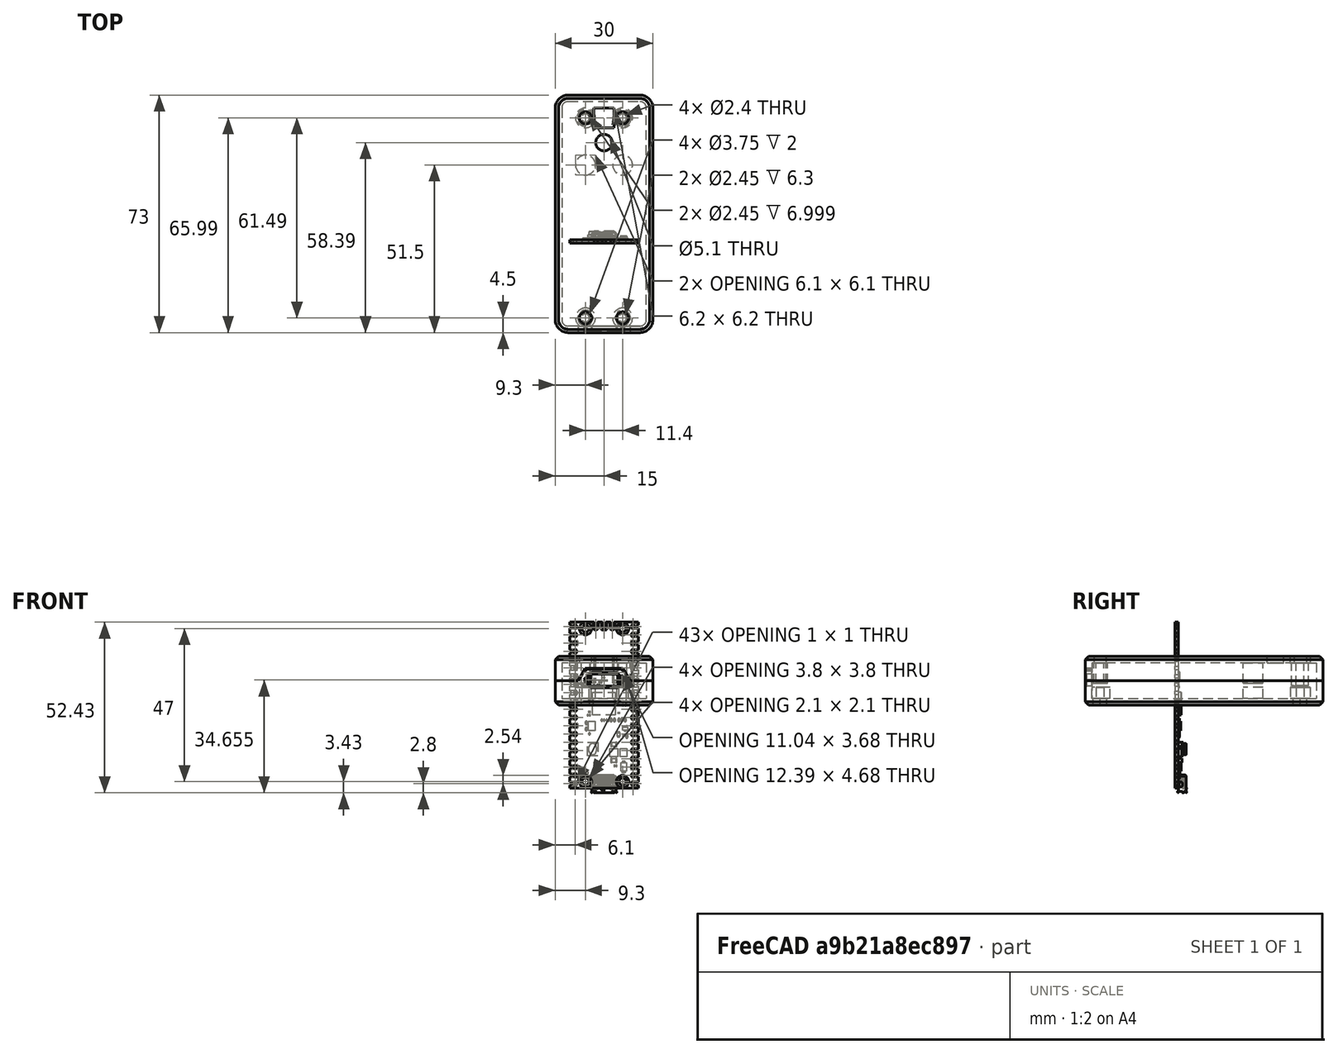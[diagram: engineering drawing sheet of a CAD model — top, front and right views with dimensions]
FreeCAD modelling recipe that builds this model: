
FCSTD DOCUMENT  (FreeCAD 2022.111R30764 (Git))
Label: case
License: All rights reserved
LicenseURL: http://en.wikipedia.org/wiki/All_rights_reserved
objects: Part::Feature×44, Sketcher::SketchObject×18, PartDesign::SubShapeBinder×13, PartDesign::Pocket×9, PartDesign::Pad×7, PartDesign::Chamfer×5, PartDesign::Extrusion×4, PartDesign::Body×4, App::Part×2, PartDesign::Fillet×2, PartDesign::Plane×2, Mesh::Feature×2, PartDesign::Solid×2, PartDesign::Thickness×1, PartDesign::ShapeBinder×1, PartDesign::Split×1
note: 170 computed .brp shape members not serialized (recipe doc carries the construction recipe); baked Part::Feature solids carry a one-line shape summary decoded from their .brp

FEATURE [Part::Feature] Part__Feature  label="PCB, Raspberry Pi Pico-R3"
  TreeRank = 93
  shape: bbox 21 x 1 x 51 mm, 416 faces (baked)
FEATURE [Part::Feature] Part__Feature001  label="MicroUSB Port, Raspberry Pi Pico-R3"
  Placement = pos=(0,0.5,-24.35) rot=(0,1,0;3.14159rad)
  TreeRank = 94
  shape: bbox 8 x 2.95 x 5.462 mm, 1230 faces, 7 solids (baked)
FEATURE [Part::Feature] Part__Feature002  label="RP2040 Microcontroller, Raspberry Pi Pico-R3"
  Placement = pos=(0,0.5,0.5) rot=(0,0,1;0rad)
  TreeRank = 95
  shape: bbox 7 x 0.9 x 7 mm, 6 faces (baked)
FEATURE [Part::Feature] Part__Feature003  label="SW1, Tact Switch, Raspberry Pi Pico-R3"
  Placement = pos=(-3.5,0.5,-13.5) rot=(0,0,1;0rad)
  TreeRank = 96
  shape: bbox 3.2 x 2.5 x 4.25 mm, 17 faces (baked)
FEATURE [Part::Feature] Part__Feature004  label="D1, Diode, Schottky, Raspberry Pi Pico-R3"
  Placement = pos=(6,0.5,-19) rot=(0,0,1;0rad)
  TreeRank = 97
  shape: bbox 1.65 x 0.95 x 3.6 mm, 14 faces (baked)
FEATURE [Part::Feature] Part__Feature005  label="D2, QSME-C194, LED, Raspberry Pi Pico-R3"
  Placement = pos=(-5.8,0.5,-20.8) rot=(0,0,1;0rad)
  TreeRank = 98
  shape: bbox 1.6 x 0.55 x 0.8 mm, 6 faces (baked)
FEATURE [Part::Feature] Part__Feature006  label="L1, Inductor, Raspberry Pi Pico-R3"
  Placement = pos=(6,0.5,-14.6) rot=(0,0,1;0rad)
  TreeRank = 99
  shape: bbox 2 x 1.2 x 2.5 mm, 6 faces (baked)
FEATURE [Part::Feature] Part__Feature007  label="U2, RT6150B-33GQW, Buck Boost Converter, Raspberry Pi Pico-R3"
  Placement = pos=(3,0.5,-14.6) rot=(0,0,1;0rad)
  TreeRank = 100
  shape: bbox 2.5 x 0.8 x 2.5 mm, 6 faces (baked)
FEATURE [Part::Feature] Part__Feature008  label="U3, W25Q16JVUXIQ, Serial NOR Flash 16 Mbit, Raspberry Pi Pico-R3"
  Placement = pos=(-3.8,0.5,-6.4) rot=(0,0,1;0rad)
  TreeRank = 101
  shape: bbox 2 x 0.8 x 3 mm, 6 faces (baked)
FEATURE [Part::Feature] Part__Feature009  label="Q1, MOSFET, DMG1012T, Raspberry Pi Pico-R3"
  Placement = pos=(6.5,0.5,-7.2) rot=(0,0,1;0rad)
  TreeRank = 102
  shape: bbox 1.6 x 0.6 x 1.8 mm, 18 faces (baked)
FEATURE [Part::Feature] Part__Feature010  label="X1, X12M000000S096, 12 Mhz Crystal Resonator, Raspberry Pi Pico-R3"
  Placement = pos=(-2.2,0.5,9) rot=(0,0,1;0rad)
  TreeRank = 103
  shape: bbox 3.2 x 0.6 x 2.5 mm, 18 faces (baked)
FEATURE [Part::Feature] Part__Feature011  label="SMD Resistor, Configurable, Raspberry Pi Pico-R3_R1"
  Placement = pos=(6.2,0.5,1) rot=(0,1,0;1.5708rad)
  TreeRank = 104
  shape: bbox 1 x 0.35 x 0.5 mm, 18 faces, 3 solids (baked)
FEATURE [Part::Feature] Part__Feature012  label="SMD Resistor, Configurable, Raspberry Pi Pico-R3_R2"
  Placement = pos=(3.5,0.5,-18.6) rot=(0,1,0;1.5708rad)
  TreeRank = 105
  shape: bbox 1 x 0.35 x 0.5 mm, 18 faces, 3 solids (baked)
FEATURE [Part::Feature] Part__Feature013  label="SMD Resistor, Configurable, Raspberry Pi Pico-R3_R3"
  Placement = pos=(-2.7,0.5,-17.8) rot=(0,1,0;1.5708rad)
  TreeRank = 106
  shape: bbox 1 x 0.35 x 0.5 mm, 18 faces, 3 solids (baked)
FEATURE [Part::Feature] Part__Feature014  label="SMD Resistor, Configurable, Raspberry Pi Pico-R3_R4"
  Placement = pos=(-5.5,0.5,-5.4) rot=(0,1,0;3.14159rad)
  TreeRank = 107
  shape: bbox 0.5 x 0.35 x 1 mm, 18 faces, 3 solids (baked)
FEATURE [Part::Feature] Part__Feature015  label="SMD Resistor, Configurable, Raspberry Pi Pico-R3_R5"
  Placement = pos=(7,0.5,-9.6) rot=(0,1,0;3.14159rad)
  TreeRank = 108
  shape: bbox 0.5 x 0.35 x 1 mm, 18 faces, 3 solids (baked)
FEATURE [Part::Feature] Part__Feature016  label="SMD Resistor, Configurable, Raspberry Pi Pico-R3_R6"
  Placement = pos=(6.5,0.5,-4.6) rot=(0,1,0;3.14159rad)
  TreeRank = 109
  shape: bbox 0.5 x 0.35 x 1 mm, 18 faces, 3 solids (baked)
FEATURE [Part::Feature] Part__Feature017  label="SMD Resistor, Configurable, Raspberry Pi Pico-R3_R7"
  Placement = pos=(4.5,0.5,-9) rot=(0,1,0;3.14159rad)
  TreeRank = 110
  shape: bbox 0.8 x 0.45 x 1.6 mm, 18 faces, 3 solids (baked)
FEATURE [Part::Feature] Part__Feature018  label="SMD Resistor, Configurable, Raspberry Pi Pico-R3_R8"
  Placement = pos=(-2.7,0.5,-18.8) rot=(0,1,0;1.5708rad)
  TreeRank = 111
  shape: bbox 1 x 0.35 x 0.5 mm, 18 faces, 3 solids (baked)
FEATURE [Part::Feature] Part__Feature019  label="SMD Resistor, Configurable, Raspberry Pi Pico-R3_R9"
  Placement = pos=(5.5,0.5,-4.6) rot=(0,1,0;3.14159rad)
  TreeRank = 112
  shape: bbox 0.5 x 0.35 x 1 mm, 18 faces, 3 solids (baked)
FEATURE [Part::Feature] Part__Feature020  label="SMD Resistor, Configurable, Raspberry Pi Pico-R3_R10"
  Placement = pos=(6.2,0.5,-1e-16) rot=(0,1,0;1.5708rad)
  TreeRank = 113
  shape: bbox 1 x 0.35 x 0.5 mm, 18 faces, 3 solids (baked)
FEATURE [Part::Feature] Part__Feature021  label="SMD Resistor, Configurable, Raspberry Pi Pico-R3_R11"
  Placement = pos=(-5.5,0.5,-7.4) rot=(0,0,1;0rad)
  TreeRank = 114
  shape: bbox 0.5 x 0.35 x 1 mm, 18 faces, 3 solids (baked)
FEATURE [Part::Feature] Part__Feature022  label="SMD Resistor, Configurable, Raspberry Pi Pico-R3_R12"
  Placement = pos=(0.8,0.5,-4.6) rot=(0,1,0;3.14159rad)
  TreeRank = 115
  shape: bbox 0.3 x 0.23 x 0.6 mm, 18 faces, 3 solids (baked)
FEATURE [Part::Feature] Part__Feature023  label="SMD Resistor, Configurable, Raspberry Pi Pico-R3_R13"
  Placement = pos=(1.4,0.5,-4.6) rot=(0,1,0;3.14159rad)
  TreeRank = 116
  shape: bbox 0.3 x 0.23 x 0.6 mm, 18 faces, 3 solids (baked)
FEATURE [Part::Feature] Part__Feature024  label="SMD Resistor, Configurable, Raspberry Pi Pico-R3_R14"
  Placement = pos=(-1.1,0.5,7) rot=(0,1,0;1.5708rad)
  TreeRank = 117
  shape: bbox 1 x 0.35 x 0.5 mm, 18 faces, 3 solids (baked)
FEATURE [Part::Feature] Part__Feature025  label="SMD Resistor, Configurable, Raspberry Pi Pico-R3_R15"
  Placement = pos=(-1.7,0.5,6.2) rot=(0,1,0;1.5708rad)
  TreeRank = 118
  shape: bbox 1 x 0.35 x 0.5 mm, 18 faces, 3 solids (baked)
FEATURE [Part::Feature] Part__Feature026  label="SMD Capacitor, Configurable, Raspberry Pi Pico-R3_C1"
  Placement = pos=(3,0.5,-17) rot=(0,1,0;1.5708rad)
  TreeRank = 119
  shape: bbox 2 x 1.25 x 1.25 mm, 18 faces, 3 solids (baked)
FEATURE [Part::Feature] Part__Feature027  label="SMD Capacitor, Configurable, Raspberry Pi Pico-R3_C2"
  Placement = pos=(3,0.5,-12) rot=(0,1,0;1.5708rad)
  TreeRank = 120
  shape: bbox 2 x 1.25 x 1.25 mm, 18 faces, 3 solids (baked)
FEATURE [Part::Feature] Part__Feature028  label="SMD Capacitor, Configurable, Raspberry Pi Pico-R3_C3"
  Placement = pos=(6,0.5,-9.4) rot=(0,0,1;0rad)
  TreeRank = 121
  shape: bbox 0.3 x 0.3 x 0.6 mm, 18 faces, 3 solids (baked)
FEATURE [Part::Feature] Part__Feature029  label="SMD Capacitor, Configurable, Raspberry Pi Pico-R3_C4"
  Placement = pos=(-4.5,0.5,-2.1) rot=(0,-1,0;1.5708rad)
  TreeRank = 122
  shape: bbox 0.6 x 0.3 x 0.3 mm, 18 faces, 3 solids (baked)
FEATURE [Part::Feature] Part__Feature030  label="SMD Capacitor, Configurable, Raspberry Pi Pico-R3_C5"
  Placement = pos=(-4.5,0.5,1.5) rot=(0,-1,0;1.5708rad)
  TreeRank = 123
  shape: bbox 0.6 x 0.3 x 0.3 mm, 18 faces, 3 solids (baked)
FEATURE [Part::Feature] Part__Feature031  label="SMD Capacitor, Configurable, Raspberry Pi Pico-R3_C6"
  Placement = pos=(4.6,0.5,1.9) rot=(0,1,0;0.785398rad)
  TreeRank = 124
  shape: bbox 0.6364 x 0.3 x 0.6364 mm, 18 faces, 3 solids (baked)
FEATURE [Part::Feature] Part__Feature032  label="SMD Capacitor, Configurable, Raspberry Pi Pico-R3_C7"
  Placement = pos=(4.5,0.5,-2.4) rot=(0,-1,0;1.5708rad)
  TreeRank = 125
  shape: bbox 0.6 x 0.3 x 0.3 mm, 18 faces, 3 solids (baked)
FEATURE [Part::Feature] Part__Feature033  label="SMD Capacitor, Configurable, Raspberry Pi Pico-R3_C8"
  Placement = pos=(0,0.5,5.5) rot=(0,0,1;0rad)
  TreeRank = 126
  shape: bbox 0.3 x 0.3 x 0.6 mm, 18 faces, 3 solids (baked)
FEATURE [Part::Feature] Part__Feature034  label="SMD Capacitor, Configurable, Raspberry Pi Pico-R3_C9"
  Placement = pos=(0.8,0.5,5.5) rot=(0,0,1;0rad)
  TreeRank = 127
  shape: bbox 0.3 x 0.3 x 0.6 mm, 18 faces, 3 solids (baked)
FEATURE [Part::Feature] Part__Feature035  label="SMD Capacitor, Configurable, Raspberry Pi Pico-R3_C10"
  Placement = pos=(0,0.5,-4.6) rot=(0,0,1;0rad)
  TreeRank = 128
  shape: bbox 0.3 x 0.3 x 0.6 mm, 18 faces, 3 solids (baked)
FEATURE [Part::Feature] Part__Feature036  label="SMD Capacitor, Configurable, Raspberry Pi Pico-R3_C11"
  Placement = pos=(-0.7,0.5,-4.6) rot=(0,0,1;0rad)
  TreeRank = 129
  shape: bbox 0.3 x 0.3 x 0.6 mm, 18 faces, 3 solids (baked)
FEATURE [Part::Feature] Part__Feature037  label="SMD Capacitor, Configurable, Raspberry Pi Pico-R3_C12"
  Placement = pos=(2.2,0.5,-4.6) rot=(0,0,1;0rad)
  TreeRank = 130
  shape: bbox 0.5 x 0.5 x 1 mm, 18 faces, 3 solids (baked)
FEATURE [Part::Feature] Part__Feature038  label="SMD Capacitor, Configurable, Raspberry Pi Pico-R3_C13"
  Placement = pos=(4.6,0.5,-4.6) rot=(0,0,1;0rad)
  TreeRank = 131
  shape: bbox 0.5 x 0.5 x 1 mm, 18 faces, 3 solids (baked)
FEATURE [Part::Feature] Part__Feature039  label="SMD Capacitor, Configurable, Raspberry Pi Pico-R3_C14"
  Placement = pos=(3.2,0.5,-4.6) rot=(0,0,1;0rad)
  TreeRank = 132
  shape: bbox 0.5 x 0.5 x 1 mm, 18 faces, 3 solids (baked)
FEATURE [Part::Feature] Part__Feature040  label="SMD Capacitor, Configurable, Raspberry Pi Pico-R3_C15"
  Placement = pos=(-4.5,0.5,-8.8) rot=(0,0,1;0rad)
  TreeRank = 133
  shape: bbox 0.3 x 0.3 x 0.6 mm, 18 faces, 3 solids (baked)
FEATURE [Part::Feature] Part__Feature041  label="SMD Capacitor, Configurable, Raspberry Pi Pico-R3_C16"
  Placement = pos=(-4.6,0.5,9.6) rot=(0,0,1;0rad)
  TreeRank = 134
  shape: bbox 0.3 x 0.3 x 0.6 mm, 18 faces, 3 solids (baked)
FEATURE [Part::Feature] Part__Feature042  label="SMD Capacitor, Configurable, Raspberry Pi Pico-R3_C17"
  Placement = pos=(0,0.5,8.5) rot=(0,0,1;0rad)
  TreeRank = 135
  shape: bbox 0.3 x 0.3 x 0.6 mm, 18 faces, 3 solids (baked)
FEATURE [Part::Feature] Part__Feature043  label="SMD Capacitor, Configurable, Raspberry Pi Pico-R3_C18"
  Placement = pos=(-4.7,0.5,-3.1) rot=(0,-1,0;1.5708rad)
  TreeRank = 136
  shape: bbox 1 x 0.5 x 0.5 mm, 18 faces, 3 solids (baked)
FEATURE [App::Part] Raspberry_Pi_Pico_R3  label="Raspberry Pi Pico-R3"
  ExportMode = 1
  Group = -> [Part__Feature,Part__Feature001,Part__Feature002,Part__Feature003,Part__Feature004,Part__Feature005,Part__Feature006,Part__Feature007,Part__Feature008,Part__Feature009,Part__Feature010,Part__Feature011,Part__Feature012,Part__Feature013,Part__Feature014,Part__Feature015,Part__Feature016,Part__Feature017,Part__Feature018,Part__Feature019,Part__Feature020,Part__Feature021,Part__Feature022,+21 more]
  Origin = -> Origin
  Placement = pos=(0,0,6) rot=(0,-0.707107,-0.707107;3.14159rad)
  TreeRank = 138
  _ExportChildren = -> [Part__Feature,Part__Feature001,Part__Feature002,Part__Feature003,Part__Feature004,Part__Feature005,Part__Feature006,Part__Feature007,Part__Feature008,Part__Feature009,Part__Feature010,Part__Feature011,Part__Feature012,Part__Feature013,Part__Feature014,Part__Feature015,Part__Feature016,Part__Feature017,Part__Feature018,Part__Feature019,Part__Feature020,Part__Feature021,Part__Feature022,+21 more]
  _GroupVersion = 1
FEATURE [PartDesign::SubShapeBinder] Binder  label="main_board_binder"
  BindCopyOnChange = 0
  BindMode = 0
  ClaimChildren = false
  Context = -> Part [Body.Binder.]
  FillStyle = 0
  Fuse = false
  MakeFace = true
  PartialLoad = false
  Relative = true
  Support = -> [Raspberry_Pi_Pico_R3[Part__Feature.]]
  TreeRank = 160
  _Version = 8
FEATURE [Sketcher::SketchObject] Sketch
  ExternalGeometry = -> [Binder]
  FullyConstrained = true
  MapMode = 5
  Support = -> [XY_Plane]
  TreeRank = 157
  sketch-geometry (5):
    g0: LineSegment StartX=-15 StartY=45 StartZ=0 EndX=15 EndY=45 EndZ=0
    g1: LineSegment StartX=15 StartY=45 StartZ=0 EndX=15 EndY=-28 EndZ=0
    g2: LineSegment StartX=15 StartY=-28 StartZ=0 EndX=-15 EndY=-28 EndZ=0
    g3: LineSegment StartX=-15 StartY=-28 StartZ=0 EndX=-15 EndY=45 EndZ=0
    g4: LineSegment [constr] StartX=0 StartY=0 StartZ=0 EndX=0 EndY=45 EndZ=0
  constraints (14):
    c: Coincident(g0,g1)
    c: Coincident(g1,g2)
    c: Coincident(g2,g3)
    c: Coincident(g3,g0)
    c: Horizontal(g0)
    c: Vertical(g3)
    c: Horizontal(g2)
    c: Vertical(g1)
    c: DistanceY(g-1,g0) = 45
    c: Coincident(g4,g-1)
    c: Vertical(g4)
    c: Symmetric(g0,g0,g4)
    c: DistanceX(g0,g0) = 30
    c: DistanceY(g1,g-3) = 2.5
FEATURE [PartDesign::Pad] Pad  label="case_pad"
  AddSubType = 0
  AlongSketchNormal = false
  CheckUpToFaceLimits = true
  ClaimChildren = false
  Direction = (0,0,1)
  Fit = 0
  FitJoin = 0
  InnerFit = 0
  InnerFitJoin = 0
  InnerTaperAngle = 0
  InnerTaperAngleRev = 0
  Length = 15
  Length2 = 100
  Linearize = true
  NewSolid = false
  Profile = -> Sketch
  Refine = true
  Suppress = false
  TreeRank = 158
  Type = 0
  _ProfileBasedVersion = 1
FEATURE [PartDesign::Thickness] Thickness
  AddSubType = 0
  Base = -> Pad [Face6]
  BaseFeature = -> Pad
  Intersection = false
  Join = 1
  Mode = 0
  NewSolid = false
  Refine = true
  Reversed = true
  SupportTransform = false
  Suppress = false
  TreeRank = 159
  Value = 2
FEATURE [PartDesign::SubShapeBinder] Binder001  label="feet"
  BindCopyOnChange = 0
  BindMode = 0
  ClaimChildren = false
  Context = -> Part [Body.Pad001.Binder001.]
  FillStyle = 0
  Fuse = true
  MakeFace = true
  PartialLoad = false
  Relative = true
  Support = -> [Binder[Edge472,Edge212,Edge474,Edge208,Edge476,Edge204,Edge470,Edge216]]
  TreeRank = 161
  _Version = 8
FEATURE [PartDesign::Pad] Pad001  label="feet_pad"
  AddSubType = 0
  AlongSketchNormal = false
  BaseFeature = -> Thickness
  CheckUpToFaceLimits = false
  ClaimChildren = false
  Direction = (1e-16,-2e-16,1)
  Fit = 2
  FitJoin = 0
  InnerFit = 0
  InnerFitJoin = 0
  InnerTaperAngle = 0
  InnerTaperAngleRev = 0
  Length = 10
  Length2 = 100
  Linearize = true
  NewSolid = false
  Profile = -> Binder001
  Refine = true
  Suppress = false
  TreeRank = 162
  Type = 3
  UpToFace = -> Thickness [Face11]
  _ProfileBasedVersion = 1
FEATURE [PartDesign::SubShapeBinder] Binder002  label="port"
  BindCopyOnChange = 0
  BindMode = 0
  ClaimChildren = false
  Context = -> Part [Body.Binder002.]
  FillStyle = 0
  Fuse = false
  MakeFace = true
  PartialLoad = false
  Relative = true
  Support = -> [Raspberry_Pi_Pico_R3[Part__Feature001.Edge930,Part__Feature001.Edge1032,Part__Feature001.Edge202,Part__Feature001.Edge967,Part__Feature001.Edge1002]]
  TreeRank = 163
  _Version = 8
FEATURE [Sketcher::SketchObject] Sketch001
  ExternalGeometry = -> [Binder002]
  FullyConstrained = true
  MapMode = 5
  Placement = pos=(0,0,0) rot=(1,0,0;1.5708rad)
  Support = -> [XZ_Plane]
  TreeRank = 164
  sketch-geometry (11):
    g0: LineSegment StartX=-3.75 StartY=9.56644 StartZ=0 EndX=-5.51777 EndY=7.79867 EndZ=0
    g1: LineSegment StartX=-5.51777 StartY=7.79867 StartZ=0 EndX=-3.9108 EndY=5.88356 EndZ=0
    g2: LineSegment StartX=-3.9108 StartY=5.88356 StartZ=0 EndX=3.9108 EndY=5.88356 EndZ=0
    g3: LineSegment StartX=3.9108 StartY=5.88356 StartZ=0 EndX=5.51777 EndY=7.79867 EndZ=0
    g4: LineSegment StartX=5.51777 StartY=7.79867 StartZ=0 EndX=3.75 EndY=9.56644 EndZ=0
    g5: LineSegment StartX=3.75 StartY=9.56644 StartZ=0 EndX=-3.75 EndY=9.56644 EndZ=0
    g6: GeomPoint [constr] X=2.3e-15 Y=9.18253 Z=0
    g7: LineSegment [constr] StartX=-0.23 StartY=6.26747 StartZ=0 EndX=0.23 EndY=6.26747 EndZ=0
    g8: LineSegment [constr] StartX=2.7e-15 StartY=9.56644 StartZ=0 EndX=2.7e-15 EndY=5.88356 EndZ=0
    g9: GeomPoint [constr] X=3.2e-15 Y=6.26747 Z=0
    g10: GeomPoint [constr] X=2.7e-15 Y=7.725 Z=0
  constraints (25):
    c: Coincident(g1,g0)
    c: Horizontal(g2)
    c: Coincident(g3,g2)
    c: Coincident(g4,g3)
    c: Coincident(g5,g0)
    c: Horizontal(g5)
    c: Coincident(g4,g5)
    c: Angle(g4,g3) = 1.65806
    c: Angle(g1,g0) = 1.65806
    c: Equal(g0,g1)
    c: Equal(g1,g4)
    c: Equal(g4,g3)
    c: Distance(g0,g0) = 2.5
    c: Angle(g0,g5) = 2.35619
    c: DistanceX(g0,g4) = 7.5
    c: Symmetric(g-3,g-3,g6)
    c: Coincident(g7,g-6)
    c: Coincident(g7,g-5)
    c: PointOnObject(g8,g2)
    c: Vertical(g8)
    c: Symmetric(g4,g0,g8)
    c: Symmetric(g-5,g-6,g9)
    c: Symmetric(g8,g8,g10)
    c: Coincident(g2,g1)
    c: Symmetric(g6,g9,g10)
FEATURE [PartDesign::Pocket] Pocket  label="port_pocket"
  AddSubType = 1
  BaseFeature = -> Pad001
  CheckUpToFaceLimits = true
  ClaimChildren = false
  Fit = 0
  FitJoin = 0
  InnerFit = 0
  InnerFitJoin = 0
  InnerTaperAngle = 0
  InnerTaperAngleRev = 0
  Length = 0
  Length2 = 100
  Linearize = true
  NewSolid = false
  Profile = -> Sketch001
  Refine = true
  Reversed = true
  Suppress = false
  TreeRank = 165
  Type = 1
  _ProfileBasedVersion = 1
  _Version = 1
FEATURE [PartDesign::SubShapeBinder] Binder003  label="Binder003(port_pocket)..."
  BindCopyOnChange = 0
  BindMode = 0
  ClaimChildren = false
  Context = -> Part [Body.Binder003.]
  FillStyle = 0
  Fuse = false
  MakeFace = true
  PartialLoad = false
  Relative = true
  Support = -> [Pocket[Edge7,Edge12,Edge10,Edge4]]
  TreeRank = 166
  _Version = 8
FEATURE [PartDesign::Pad] Pad002  label="top"
  AddSubType = 0
  AlongSketchNormal = false
  BaseFeature = -> Pocket
  CheckUpToFaceLimits = true
  ClaimChildren = false
  Direction = (0,0,1)
  Fit = 0
  FitJoin = 0
  InnerFit = 0
  InnerFitJoin = 0
  InnerTaperAngle = 0
  InnerTaperAngleRev = 0
  Length = 2
  Length2 = 100
  Linearize = true
  NewSolid = false
  Profile = -> Binder003
  Refine = true
  Reversed = true
  Suppress = false
  TreeRank = 167
  Type = 0
  _ProfileBasedVersion = 1
FEATURE [PartDesign::Fillet] Fillet
  AddSubType = 0
  Base = -> Pad002 [Edge9,Edge10,Edge5,Edge7]
  BaseFeature = -> Pad002
  NewSolid = false
  Radius = 4
  Refine = true
  SupportTransform = false
  Suppress = false
  TreeRank = 168
FEATURE [PartDesign::Fillet] Fillet001
  AddSubType = 0
  Base = -> Fillet [Edge54,Edge44,Edge58,Edge74]
  BaseFeature = -> Fillet
  NewSolid = false
  Radius = 2
  Refine = true
  SupportTransform = false
  Suppress = false
  TreeRank = 169
FEATURE [PartDesign::Chamfer] Chamfer
  AddSubType = 0
  Angle = 45
  Base = -> Fillet001 [Edge86,Edge75]
  BaseFeature = -> Fillet001
  ChamferType = 0
  FlipDirection = false
  NewSolid = false
  Refine = true
  Size = 1
  Size2 = 1
  SupportTransform = false
  Suppress = false
  TreeRank = 170
FEATURE [PartDesign::Chamfer] Chamfer001
  AddSubType = 0
  Angle = 45
  Base = -> Chamfer [Edge5,Edge6,Edge7,Edge8,Edge9,Edge10]
  BaseFeature = -> Chamfer
  ChamferType = 0
  FlipDirection = false
  NewSolid = false
  Refine = true
  Size = 0.5
  Size2 = 1
  SupportTransform = false
  Suppress = false
  TreeRank = 171
FEATURE [PartDesign::ShapeBinder] ShapeBinder
  Support = -> [Chamfer001]
  TraceSupport = false
  TreeRank = 185
FEATURE [Sketcher::SketchObject] Sketch002
  ExternalGeometry = -> [ShapeBinder]
  FullyConstrained = true
  MapMode = 5
  Placement = pos=(-13,0,0) rot=(0.57735,0.57735,0.57735;2.0944rad)
  Support = -> [ShapeBinder]
  TreeRank = 186
  sketch-geometry (1):
    g0: LineSegment StartX=41 StartY=7.5 StartZ=0 EndX=-24 EndY=7.5 EndZ=0
  constraints (3):
    c: PointOnObject(g0,g-3)
    c: Horizontal(g0)
    c: Symmetric(g-4,g-4,g0)
FEATURE [PartDesign::Extrusion] Extrusion
  AddSubType = 0
  AlongSketchNormal = false
  CheckUpToFaceLimits = true
  ClaimChildren = false
  Direction = (1,0,0)
  Fit = 0
  FitJoin = 0
  InnerFit = 0
  InnerFitJoin = 0
  InnerTaperAngle = 0
  InnerTaperAngleRev = 0
  Length = 10
  Length2 = 100
  Linearize = true
  NewSolid = false
  Profile = -> Sketch002
  Refine = true
  Reversed = true
  Suppress = false
  TreeRank = 187
  Type = 0
  _ProfileBasedVersion = 1
FEATURE [Sketcher::SketchObject] Sketch003
  ExternalGeometry = -> [ShapeBinder]
  FullyConstrained = true
  MapMode = 5
  Placement = pos=(13,0,0) rot=(0.57735,-0.57735,-0.57735;2.0944rad)
  Support = -> [ShapeBinder]
  TreeRank = 188
  sketch-geometry (1):
    g0: LineSegment StartX=24 StartY=7.5 StartZ=0 EndX=-41 EndY=7.5 EndZ=0
  constraints (3):
    c: PointOnObject(g0,g-3)
    c: Horizontal(g0)
    c: Symmetric(g-4,g-4,g0)
FEATURE [PartDesign::Extrusion] Extrusion001
  AddSubType = 0
  AlongSketchNormal = false
  CheckUpToFaceLimits = true
  ClaimChildren = false
  Direction = (-1,0,0)
  Fit = 0
  FitJoin = 0
  InnerFit = 0
  InnerFitJoin = 0
  InnerTaperAngle = 0
  InnerTaperAngleRev = 0
  Length = 10
  Length2 = 100
  Linearize = true
  NewSolid = false
  Profile = -> Sketch003
  Refine = true
  Reversed = true
  Suppress = false
  TreeRank = 189
  Type = 0
  _ProfileBasedVersion = 1
FEATURE [PartDesign::Plane] DatumPlane
  AttachmentOffset = pos=(0,0,0) rot=(0,1,0;1.5708rad)
  Length = 10
  MapMode = 45
  MinimumLength = 10
  MinimumWidth = 10
  Placement = pos=(0,-24,7.5) rot=(0,0.707107,0.707107;3.14159rad)
  ResizeMode = 0
  Support = -> [Extrusion,Extrusion001]
  TreeRank = 190
  Width = 10
FEATURE [Sketcher::SketchObject] Sketch004
  ExternalGeometry = -> [Extrusion,Extrusion001,ShapeBinder]
  FullyConstrained = true
  MapMode = 5
  Placement = pos=(0,-24,7.5) rot=(0,0.707107,0.707107;3.14159rad)
  Support = -> [DatumPlane]
  TreeRank = 191
  sketch-geometry (5):
    g0: LineSegment StartX=23 StartY=0 StartZ=0 EndX=8 EndY=4e-16 EndZ=0
    g1: LineSegment StartX=-23 StartY=0 StartZ=0 EndX=-8 EndY=0 EndZ=0
    g2: LineSegment StartX=-8 StartY=0 StartZ=0 EndX=-5.77348 EndY=3.85644 EndZ=0
    g3: LineSegment StartX=-5.77348 StartY=3.85644 StartZ=0 EndX=5.77348 EndY=3.85644 EndZ=0
    g4: LineSegment StartX=5.77348 StartY=3.85644 StartZ=0 EndX=8 EndY=4e-16 EndZ=0
  constraints (14):
    c: Coincident(g0,g-3)
    c: PointOnObject(g0,g-1)
    c: Coincident(g1,g-4)
    c: PointOnObject(g1,g-1)
    c: Coincident(g2,g1)
    c: Coincident(g3,g2)
    c: Horizontal(g3)
    c: Coincident(g4,g3)
    c: Coincident(g4,g0)
    c: Angle(g3,g4) = 2.0944
    c: Angle(g2,g3) = 2.0944
    c: DistanceX(g0,g0) = 15
    c: DistanceX(g1,g1) = 15
    c: DistanceY(g-7,g2) = 1.29
FEATURE [PartDesign::Extrusion] Extrusion002
  AddSubType = 0
  AlongSketchNormal = false
  CheckUpToFaceLimits = true
  ClaimChildren = false
  Direction = (0,1,2e-16)
  Fit = 0
  FitJoin = 0
  InnerFit = 0
  InnerFitJoin = 0
  InnerTaperAngle = 0
  InnerTaperAngleRev = 0
  Length = 10
  Length2 = 100
  Linearize = true
  NewSolid = false
  Placement = pos=(0,-24,7.5) rot=(0,0.707107,0.707107;3.14159rad)
  Profile = -> Sketch004
  Refine = true
  Reversed = true
  Suppress = false
  TreeRank = 192
  Type = 0
  _ProfileBasedVersion = 1
FEATURE [PartDesign::Plane] DatumPlane001
  AttachmentOffset = pos=(0,0,0) rot=(0,1,0;1.5708rad)
  Length = 46
  MapMode = 45
  MinimumLength = 10
  MinimumWidth = 10
  Placement = pos=(0,41,7.5) rot=(0,0.707107,0.707107;3.14159rad)
  ResizeMode = 0
  Support = -> [Extrusion,Extrusion001]
  TreeRank = 193
  Width = 10
FEATURE [Sketcher::SketchObject] Sketch005
  ExternalGeometry = -> [Extrusion001,Extrusion]
  FullyConstrained = true
  MapMode = 5
  Placement = pos=(0,41,7.5) rot=(0,0.707107,0.707107;3.14159rad)
  Support = -> [DatumPlane001]
  TreeRank = 194
  sketch-geometry (1):
    g0: LineSegment StartX=-23 StartY=0 StartZ=0 EndX=23 EndY=0 EndZ=0
  constraints (2):
    c: Coincident(g0,g-3)
    c: Coincident(g0,g-4)
FEATURE [PartDesign::Extrusion] Extrusion003
  AddSubType = 0
  AlongSketchNormal = false
  CheckUpToFaceLimits = true
  ClaimChildren = false
  Direction = (0,1,2e-16)
  Fit = 0
  FitJoin = 0
  InnerFit = 0
  InnerFitJoin = 0
  InnerTaperAngle = 0
  InnerTaperAngleRev = 0
  Length = 10
  Length2 = 100
  Linearize = true
  NewSolid = false
  Placement = pos=(0,41,7.5) rot=(0,0.707107,0.707107;3.14159rad)
  Profile = -> Sketch005
  Refine = true
  Suppress = false
  TreeRank = 195
  Type = 0
  _ProfileBasedVersion = 1
FEATURE [PartDesign::SubShapeBinder] Binder004  label="Binder004(Extrusion)..."
  BindCopyOnChange = 0
  BindMode = 0
  ClaimChildren = false
  Context = -> Body001 [Binder004.]
  FillStyle = 0
  Fuse = true
  MakeFace = true
  PartialLoad = false
  Refine = true
  Relative = true
  Support = -> [Extrusion,Extrusion002,Extrusion003,Extrusion001]
  TreeRank = 196
  _Version = 8
FEATURE [PartDesign::Body] Body001  label="sep_plane"
  AutoGroupSolids = false
  ExportMode = 0
  Group = -> [ShapeBinder,Sketch002,Extrusion,Sketch003,Extrusion001,DatumPlane,Sketch004,Extrusion002,DatumPlane001,Sketch005,Extrusion003,Binder004]
  Origin = -> Origin003
  TreeRank = 184
  _ExportChildren = -> [ShapeBinder,Sketch002,Extrusion,Sketch003,Extrusion001,DatumPlane,Sketch004,Extrusion002,DatumPlane001,Sketch005,Extrusion003,Binder004]
  _GroupVersion = 1
FEATURE [PartDesign::SubShapeBinder] Import  label="Import(*Extrusion...)"
  BindCopyOnChange = 0
  BindMode = 0
  ClaimChildren = false
  Context = -> Part [Body.Import.]
  FillStyle = 0
  Fuse = false
  MakeFace = false
  PartialLoad = false
  Relative = true
  Support = -> [Body001[Binder004.]]
  TreeRank = 198
  _Version = 8
FEATURE [PartDesign::SubShapeBinder] BaseFeature  label="BaseFeature(Split_i0)"
  BindCopyOnChange = 0
  BindMode = 0
  ClaimChildren = false
  Context = -> Body002 [BaseFeature.]
  FillStyle = 0
  Fuse = true
  MakeFace = true
  PartialLoad = false
  Relative = true
  Support = -> [Part[Body.Split_i0.]]
  TreeRank = 216
  _Version = 8
FEATURE [PartDesign::SubShapeBinder] BaseFeature001  label="BaseFeature001(Split_i1)"
  BindCopyOnChange = 0
  BindMode = 0
  ClaimChildren = false
  Context = -> Body003 [BaseFeature001.]
  FillStyle = 0
  Fuse = true
  MakeFace = true
  PartialLoad = false
  Relative = true
  Support = -> [Part[Body.Split_i1.]]
  TreeRank = 229
  _Version = 8
FEATURE [PartDesign::Chamfer] Chamfer002  label="fixed_cham"
  AddSubType = 0
  Angle = 45
  Base = -> BaseFeature [Edge135]
  BaseFeature = -> BaseFeature
  ChamferType = 0
  FlipDirection = false
  NewSolid = false
  Refine = true
  Size = 0.01
  Size2 = 1
  SupportTransform = false
  Suppress = false
  TreeRank = 230
FEATURE [PartDesign::Chamfer] Chamfer003  label="fix_cham"
  AddSubType = 0
  Angle = 45
  Base = -> BaseFeature001 [Edge46]
  BaseFeature = -> BaseFeature001
  ChamferType = 0
  FlipDirection = false
  NewSolid = false
  Refine = true
  Size = 0.01
  Size2 = 1
  SupportTransform = false
  Suppress = false
  TreeRank = 231
FEATURE [Sketcher::SketchObject] Sketch006
  ExternalGeometry = -> [Chamfer003]
  FullyConstrained = true
  MapMode = 5
  Placement = pos=(0,0,15) rot=(0,0,1;0rad)
  Support = -> [Chamfer003]
  TreeRank = 232
  sketch-geometry (9):
    g0: LineSegment [constr] StartX=-13.99 StartY=37.99 StartZ=0 EndX=13.99 EndY=37.99 EndZ=0
    g1: GeomPoint [constr] X=4e-16 Y=37.99 Z=0
    g2: LineSegment [constr] StartX=4e-16 StartY=37.99 StartZ=0 EndX=4e-16 EndY=43.99 EndZ=0
    g3: GeomPoint [constr] X=-3.1 Y=37.99 Z=0
    g4: GeomPoint [constr] X=3.1 Y=37.99 Z=0
    g5: LineSegment StartX=-3.1 StartY=41.09 StartZ=0 EndX=3.1 EndY=41.09 EndZ=0
    g6: LineSegment StartX=3.1 StartY=41.09 StartZ=0 EndX=3.1 EndY=34.89 EndZ=0
    g7: LineSegment StartX=3.1 StartY=34.89 StartZ=0 EndX=-3.1 EndY=34.89 EndZ=0
    g8: LineSegment StartX=-3.1 StartY=34.89 StartZ=0 EndX=-3.1 EndY=41.09 EndZ=0
  constraints (21):
    c: PointOnObject(g0,g-3)
    c: PointOnObject(g0,g-4)
    c: Horizontal(g0)
    c: Symmetric(g0,g0,g1)
    c: Coincident(g2,g1)
    c: PointOnObject(g2,g-5)
    c: Vertical(g2)
    c: DistanceY(g1,g2) = 6
    c: Symmetric(g4,g3,g1)
    c: Coincident(g5,g6)
    c: Coincident(g6,g7)
    c: Coincident(g7,g8)
    c: Coincident(g8,g5)
    c: Horizontal(g5)
    c: Horizontal(g7)
    c: Vertical(g6)
    c: Vertical(g8)
    c: DistanceX(g5,g5) = 6.2
    c: DistanceY(g6,g6) = 6.2
    c: Symmetric(g5,g6,g4)
    c: Symmetric(g5,g7,g3)
FEATURE [PartDesign::Pocket] Pocket001
  AddSubType = 1
  BaseFeature = -> Chamfer003
  CheckUpToFaceLimits = true
  ClaimChildren = false
  Fit = 0
  FitJoin = 0
  InnerFit = 0
  InnerFitJoin = 0
  InnerTaperAngle = 0
  InnerTaperAngleRev = 0
  Length = 5
  Length2 = 100
  Linearize = true
  NewSolid = false
  Profile = -> Sketch006
  Refine = true
  Suppress = false
  TreeRank = 233
  Type = 0
  _ProfileBasedVersion = 1
  _Version = 1
FEATURE [Sketcher::SketchObject] Sketch007
  ExternalGeometry = -> [Pocket001,Sketch006]
  FullyConstrained = true
  MapMode = 5
  Placement = pos=(0,0,15) rot=(0,0,1;0rad)
  Support = -> [Pocket001]
  TreeRank = 236
  sketch-geometry (3):
    g0: Circle CenterX=-5e-16 CenterY=30.39 CenterZ=0 NormalX=0 NormalY=0 NormalZ=1 AngleXU=0 Radius=2.55
    g1: GeomPoint [constr] X=-5e-16 Y=34.89 Z=0
    g2: LineSegment [constr] StartX=-5e-16 StartY=34.89 StartZ=0 EndX=-5e-16 EndY=30.39 EndZ=0
  constraints (6):
    c: Diameter(g0) = 5.1
    c: Symmetric(g-7,g-7,g1)
    c: Coincident(g2,g1)
    c: Coincident(g2,g0)
    c: Vertical(g2)
    c: DistanceY(g0,g1) = 4.5
FEATURE [PartDesign::Pocket] Pocket002
  AddSubType = 1
  BaseFeature = -> Pocket001
  CheckUpToFaceLimits = true
  ClaimChildren = false
  Fit = 0
  FitJoin = 0
  InnerFit = 0
  InnerFitJoin = 0
  InnerTaperAngle = 0
  InnerTaperAngleRev = 0
  Length = 5
  Length2 = 100
  Linearize = true
  NewSolid = false
  Profile = -> Sketch007
  Refine = true
  Suppress = false
  TreeRank = 235
  Type = 0
  _ProfileBasedVersion = 1
  _Version = 1
FEATURE [Sketcher::SketchObject] Sketch008
  ExternalGeometry = -> [Chamfer002]
  FullyConstrained = true
  MapMode = 5
  Placement = pos=(0,0,2) rot=(0,0,1;0rad)
  Support = -> [Chamfer002]
  TreeRank = 238
  sketch-geometry (4):
    g0: Circle CenterX=-5.7 CenterY=37.99 CenterZ=0 NormalX=0 NormalY=0 NormalZ=1 AngleXU=0 Radius=3.05
    g1: LineSegment [constr] StartX=-5.7 StartY=23.5 StartZ=0 EndX=-5.7 EndY=37.99 EndZ=0
    g2: Circle CenterX=5.7 CenterY=37.99 CenterZ=0 NormalX=0 NormalY=0 NormalZ=1 AngleXU=0 Radius=3.05
    g3: LineSegment [constr] StartX=5.7 StartY=23.5 StartZ=0 EndX=5.7 EndY=37.99 EndZ=0
  constraints (11):
    c: Radius(g-3) = 3.05
    c: Radius(g0) = 3.05
    c: Coincident(g1,g-4)
    c: Coincident(g1,g0)
    c: Vertical(g1)
    c: Equal(g0,g2) = 3.05
    c: Coincident(g3,g-6)
    c: Coincident(g3,g2)
    c: Vertical(g3)
    c: DistanceY(g3,g3) = 14.49
    c: DistanceY(g1,g1) = 14.49
FEATURE [PartDesign::Pad] Pad003
  AddSubType = 0
  AlongSketchNormal = false
  BaseFeature = -> Chamfer002
  CheckUpToFaceLimits = true
  ClaimChildren = false
  Direction = (0,0,1)
  Fit = 0
  FitJoin = 0
  InnerFit = 0
  InnerFitJoin = 0
  InnerTaperAngle = 0
  InnerTaperAngleRev = 0
  Length = 10
  Length2 = 100
  Linearize = true
  NewSolid = false
  Profile = -> Sketch008
  Refine = true
  Suppress = false
  TreeRank = 239
  Type = 3
  UpToFace = -> Chamfer002 [Face34]
  _ProfileBasedVersion = 1
FEATURE [Sketcher::SketchObject] Sketch009
  ExternalGeometry = -> [Pad003]
  FullyConstrained = true
  MapMode = 5
  Placement = pos=(0,0,0) rot=(1,0,0;3.14159rad)
  Support = -> [Pad003]
  TreeRank = 240
  sketch-geometry (28):
    g0: LineSegment StartX=6.9125 StartY=25.6001 StartZ=0 EndX=4.4875 EndY=25.6001 EndZ=0
    g1: LineSegment StartX=4.4875 StartY=25.6001 StartZ=0 EndX=3.275 EndY=23.5 EndZ=0
    g2: LineSegment StartX=3.275 StartY=23.5 StartZ=0 EndX=4.4875 EndY=21.3999 EndZ=0
    g3: LineSegment StartX=4.4875 StartY=21.3999 StartZ=0 EndX=6.9125 EndY=21.3999 EndZ=0
    g4: LineSegment StartX=6.9125 StartY=21.3999 StartZ=0 EndX=8.125 EndY=23.5 EndZ=0
    g5: LineSegment StartX=8.125 StartY=23.5 StartZ=0 EndX=6.9125 EndY=25.6001 EndZ=0
    g6: Circle [constr] CenterX=5.7 CenterY=23.5 CenterZ=0 NormalX=0 NormalY=0 NormalZ=1 AngleXU=0 Radius=2.425
    g7: LineSegment StartX=-3.275 StartY=23.5 StartZ=0 EndX=-4.4875 EndY=25.6001 EndZ=0
    g8: LineSegment StartX=-4.4875 StartY=25.6001 StartZ=0 EndX=-6.9125 EndY=25.6001 EndZ=0
    g9: LineSegment StartX=-6.9125 StartY=25.6001 StartZ=0 EndX=-8.125 EndY=23.5 EndZ=0
    g10: LineSegment StartX=-8.125 StartY=23.5 StartZ=0 EndX=-6.9125 EndY=21.3999 EndZ=0
    g11: LineSegment StartX=-6.9125 StartY=21.3999 StartZ=0 EndX=-4.4875 EndY=21.3999 EndZ=0
    g12: LineSegment StartX=-4.4875 StartY=21.3999 StartZ=0 EndX=-3.275 EndY=23.5 EndZ=0
    g13: Circle [constr] CenterX=-5.7 CenterY=23.5 CenterZ=0 NormalX=0 NormalY=0 NormalZ=1 AngleXU=0 Radius=2.425
    g14: LineSegment StartX=8.125 StartY=-37.99 StartZ=0 EndX=6.9125 EndY=-35.8899 EndZ=0
    g15: LineSegment StartX=6.9125 StartY=-35.8899 StartZ=0 EndX=4.4875 EndY=-35.8899 EndZ=0
    g16: LineSegment StartX=4.4875 StartY=-35.8899 StartZ=0 EndX=3.275 EndY=-37.99 EndZ=0
    g17: LineSegment StartX=3.275 StartY=-37.99 StartZ=0 EndX=4.4875 EndY=-40.0901 EndZ=0
    g18: LineSegment StartX=4.4875 StartY=-40.0901 StartZ=0 EndX=6.9125 EndY=-40.0901 EndZ=0
    g19: LineSegment StartX=6.9125 StartY=-40.0901 StartZ=0 EndX=8.125 EndY=-37.99 EndZ=0
    g20: Circle [constr] CenterX=5.7 CenterY=-37.99 CenterZ=0 NormalX=0 NormalY=0 NormalZ=1 AngleXU=0 Radius=2.425
    g21: LineSegment StartX=-3.275 StartY=-37.99 StartZ=0 EndX=-4.4875 EndY=-35.8899 EndZ=0
    g22: LineSegment StartX=-4.4875 StartY=-35.8899 StartZ=0 EndX=-6.9125 EndY=-35.8899 EndZ=0
    g23: LineSegment StartX=-6.9125 StartY=-35.8899 StartZ=0 EndX=-8.125 EndY=-37.99 EndZ=0
    g24: LineSegment StartX=-8.125 StartY=-37.99 StartZ=0 EndX=-6.9125 EndY=-40.0901 EndZ=0
    g25: LineSegment StartX=-6.9125 StartY=-40.0901 StartZ=0 EndX=-4.4875 EndY=-40.0901 EndZ=0
    g26: LineSegment StartX=-4.4875 StartY=-40.0901 StartZ=0 EndX=-3.275 EndY=-37.99 EndZ=0
    g27: Circle [constr] CenterX=-5.7 CenterY=-37.99 CenterZ=0 NormalX=0 NormalY=0 NormalZ=1 AngleXU=0 Radius=2.425
  constraints (64):
    c: Coincident(g0,g1)
    c: Coincident(g1,g2)
    c: Coincident(g2,g3)
    c: Coincident(g3,g4)
    c: Coincident(g4,g5)
    c: Coincident(g5,g0)
    c: Equal(g0, g1-g5) x5
    c: PointOnObject(g0,g6)
    c: PointOnObject(g1,g6)
    c: PointOnObject(g2,g6)
    c: PointOnObject(g3,g6)
    c: PointOnObject(g4,g6)
    c: PointOnObject(g5,g6)
    c: Horizontal(g0)
    c: Diameter(g6) = 4.85
    c: Coincident(g6,g-7)
    c: Coincident(g7,g8)
    c: Coincident(g8,g9)
    c: Coincident(g9,g10)
    c: Coincident(g10,g11)
    c: Coincident(g11,g12)
    c: Coincident(g12,g7)
    c: Equal(g7, g8-g12) x5
    c: PointOnObject(g7,g13)
    c: PointOnObject(g8,g13)
    c: PointOnObject(g9,g13)
    c: PointOnObject(g10,g13)
    c: PointOnObject(g11,g13)
    c: PointOnObject(g12,g13)
    c: Coincident(g13,g-8)
    c: Horizontal(g8)
    c: Diameter(g13) = 4.85
    c: Coincident(g14,g15)
    c: Coincident(g15,g16)
    c: Coincident(g16,g17)
    c: Coincident(g17,g18)
    c: Coincident(g18,g19)
    c: Coincident(g19,g14)
    c: Equal(g14, g15-g19) x5
    c: PointOnObject(g14,g20)
    c: PointOnObject(g15,g20)
    c: PointOnObject(g16,g20)
    c: PointOnObject(g17,g20)
    c: PointOnObject(g18,g20)
    c: PointOnObject(g19,g20)
    c: Coincident(g20,g-3)
    c: Diameter(g20) = 4.85
    c: Horizontal(g15)
    c: Coincident(g21,g22)
    c: Coincident(g22,g23)
    c: Coincident(g23,g24)
    c: Coincident(g24,g25)
    c: Coincident(g25,g26)
    c: Coincident(g26,g21)
    c: Equal(g21, g22-g26) x5
    c: PointOnObject(g21,g27)
    c: PointOnObject(g22,g27)
    c: PointOnObject(g23,g27)
    c: PointOnObject(g24,g27)
    c: PointOnObject(g25,g27)
    c: PointOnObject(g26,g27)
    c: Coincident(g27,g-4)
    c: Diameter(g27) = 4.85
    c: Horizontal(g22)
FEATURE [PartDesign::Pocket] Pocket003
  AddSubType = 1
  BaseFeature = -> Pad003
  CheckUpToFaceLimits = true
  ClaimChildren = false
  Fit = 0
  FitJoin = 0
  InnerFit = 0
  InnerFitJoin = 0
  InnerTaperAngle = 0
  InnerTaperAngleRev = 0
  Length = 2
  Length2 = 100
  Linearize = true
  NewSolid = false
  Profile = -> Sketch009
  Refine = true
  Suppress = false
  TreeRank = 241
  Type = 0
  _ProfileBasedVersion = 1
  _Version = 1
FEATURE [Sketcher::SketchObject] Sketch010
  ExternalGeometry = -> [Pocket003]
  FullyConstrained = true
  MapMode = 5
  Placement = pos=(0,0,2) rot=(1,0,0;3.14159rad)
  Support = -> [Pocket003]
  TreeRank = 242
  sketch-geometry (4):
    g0: Circle CenterX=5.7 CenterY=23.5 CenterZ=0 NormalX=0 NormalY=0 NormalZ=1 AngleXU=0 Radius=1.2
    g1: Circle CenterX=-5.7 CenterY=23.5 CenterZ=0 NormalX=0 NormalY=0 NormalZ=1 AngleXU=0 Radius=1.2
    g2: Circle CenterX=-5.7 CenterY=-37.99 CenterZ=0 NormalX=0 NormalY=0 NormalZ=1 AngleXU=0 Radius=1.2
    g3: Circle CenterX=5.7 CenterY=-37.99 CenterZ=0 NormalX=0 NormalY=0 NormalZ=1 AngleXU=0 Radius=1.2
  constraints (8):
    c: Coincident(g0,g-4)
    c: Diameter(g0) = 2.4
    c: Equal(g0,g1) = 2
    c: Coincident(g1,g-5)
    c: Coincident(g2,g-7)
    c: Diameter(g2) = 2.4
    c: Coincident(g3,g-6)
    c: Diameter(g3) = 2.4
FEATURE [PartDesign::Pocket] Pocket004
  AddSubType = 1
  BaseFeature = -> Pocket003
  CheckUpToFaceLimits = true
  ClaimChildren = false
  Fit = 0
  FitJoin = 0
  InnerFit = 0
  InnerFitJoin = 0
  InnerTaperAngle = 0
  InnerTaperAngleRev = 0
  Length = 0
  Length2 = 100
  Linearize = true
  NewSolid = false
  Profile = -> Sketch010
  Refine = true
  Suppress = false
  TreeRank = 243
  Type = 3
  UpToFace = -> Pocket003 [Face83]
  _ProfileBasedVersion = 1
  _Version = 1
FEATURE [PartDesign::Chamfer] Chamfer004
  AddSubType = 0
  Angle = 45
  Base = -> Pocket004 [Edge78,Edge61]
  BaseFeature = -> Pocket004
  ChamferType = 0
  FlipDirection = false
  NewSolid = false
  Refine = true
  Size = 1
  Size2 = 1
  SupportTransform = false
  Suppress = false
  TreeRank = 244
FEATURE [Sketcher::SketchObject] Sketch011
  FullyConstrained = false
  MapMode = 5
  Placement = pos=(1e-15,0,11.3564) rot=(0,0,1;0rad)
  Support = -> [Chamfer004]
  TreeRank = 245
  sketch-geometry (4):
    g0: LineSegment StartX=-7.92658 StartY=-24.7227 StartZ=0 EndX=8.15941 EndY=-24.7227 EndZ=0
    g1: LineSegment StartX=8.15941 StartY=-24.7227 StartZ=0 EndX=8.15941 EndY=-30.4107 EndZ=0
    g2: LineSegment StartX=8.15941 StartY=-30.4107 StartZ=0 EndX=-7.92658 EndY=-30.4107 EndZ=0
    g3: LineSegment StartX=-7.92658 StartY=-30.4107 StartZ=0 EndX=-7.92658 EndY=-24.7227 EndZ=0
  constraints (8):
    c: Coincident(g0,g1)
    c: Coincident(g1,g2)
    c: Coincident(g2,g3)
    c: Coincident(g3,g0)
    c: Horizontal(g0)
    c: Horizontal(g2)
    c: Vertical(g1)
    c: Vertical(g3)
FEATURE [PartDesign::Pocket] Pocket005
  AddSubType = 1
  BaseFeature = -> Chamfer004
  CheckUpToFaceLimits = true
  ClaimChildren = false
  Fit = 0
  FitJoin = 0
  InnerFit = 0
  InnerFitJoin = 0
  InnerTaperAngle = 0
  InnerTaperAngleRev = 0
  Length = 0.25
  Length2 = 100
  Linearize = true
  NewSolid = false
  Profile = -> Sketch011
  Refine = true
  Suppress = false
  TreeRank = 246
  Type = 0
  _ProfileBasedVersion = 1
  _Siblings = -> [Chamfer004,Pocket004,Pocket003,Pad003,Chamfer002]
  _Version = 1
FEATURE [PartDesign::Body] Body002  label="bottom_case"
  AutoGroupSolids = true
  BaseFeature = -> BaseFeature
  ExportMode = 0
  Group = -> [BaseFeature,Sketch008,Sketch009,Sketch010,Chamfer002,Pad003,Pocket003,Pocket004,Chamfer004,Sketch011,Pocket005]
  Origin = -> Origin004
  Tip = -> Pocket005
  TreeRank = 215
  _ExportChildren = -> [BaseFeature,Pocket005]
  _GroupVersion = 1
FEATURE [PartDesign::SubShapeBinder] Binder005  label="Binder005(Pocket005)..."
  BindCopyOnChange = 0
  BindMode = 0
  ClaimChildren = false
  Context = -> Body003 [Binder005.]
  FillStyle = 0
  Fuse = false
  MakeFace = true
  PartialLoad = false
  Relative = true
  Support = -> [Body002[Pocket005.Edge124,Pocket005.Edge156,Pocket005.Edge122,Pocket005.Edge155,Pocket005.Edge152,Pocket005.Edge154,Pocket005.Edge117,Pocket005.Edge116]]
  TreeRank = 251
  _Version = 8
FEATURE [Sketcher::SketchObject] Sketch012
  ExternalGeometry = -> [Binder005]
  FullyConstrained = true
  MapMode = 5
  Placement = pos=(0,0,13) rot=(1,0,0;3.14159rad)
  Support = -> [Pocket002]
  TreeRank = 252
  sketch-geometry (2):
    g0: Circle CenterX=-5.7 CenterY=-23.5 CenterZ=0 NormalX=0 NormalY=0 NormalZ=1 AngleXU=0 Radius=3.05
    g1: Circle CenterX=5.7 CenterY=-23.5 CenterZ=0 NormalX=0 NormalY=0 NormalZ=1 AngleXU=0 Radius=3.05
  constraints (4):
    c: Coincident(g0,g-11)
    c: Coincident(g1,g-13)
    c: Diameter(g0) = 6.1
    c: Diameter(g1) = 6.1
FEATURE [PartDesign::SubShapeBinder] Binder006  label="Binder006(PCB, Raspberry Pi Pico-R3)"
  BindCopyOnChange = 0
  BindMode = 0
  ClaimChildren = false
  Context = -> Body003 [Binder006.]
  FillStyle = 0
  Fuse = false
  MakeFace = true
  PartialLoad = false
  Relative = true
  Support = -> [Part[Raspberry_Pi_Pico_R3.Part__Feature.Face67]]
  TreeRank = 253
  _Version = 8
FEATURE [PartDesign::Pad] Pad004
  AddSubType = 0
  AlongSketchNormal = false
  BaseFeature = -> Pocket002
  CheckUpToFaceLimits = true
  ClaimChildren = false
  Direction = (0,0,-1)
  Fit = 0
  FitJoin = 0
  InnerFit = 0
  InnerFitJoin = 0
  InnerTaperAngle = 0
  InnerTaperAngleRev = 0
  Length = 10
  Length2 = 100
  Linearize = true
  NewSolid = false
  Offset = 0.2
  Profile = -> Sketch012
  Refine = true
  Suppress = false
  TreeRank = 254
  Type = 3
  UpToFace = -> Binder006 [Face1]
  _ProfileBasedVersion = 1
FEATURE [Sketcher::SketchObject] Sketch013
  ExternalGeometry = -> [Binder005,Pad004]
  FullyConstrained = true
  MapMode = 5
  Placement = pos=(0,0,13) rot=(1,0,0;3.14159rad)
  Support = -> [Pad004]
  TreeRank = 255
  sketch-geometry (2):
    g0: Circle CenterX=-5.7 CenterY=-37.99 CenterZ=0 NormalX=0 NormalY=0 NormalZ=1 AngleXU=0 Radius=2.6
    g1: Circle CenterX=5.7 CenterY=-37.99 CenterZ=0 NormalX=0 NormalY=0 NormalZ=1 AngleXU=0 Radius=2.6
  constraints (4):
    c: Coincident(g0,g-6)
    c: Tangent(g0,g-7)
    c: Coincident(g1,g-4)
    c: Tangent(g1,g-8)
FEATURE [PartDesign::SubShapeBinder] Import001  label="Import001(Pocket005)"
  BindCopyOnChange = 0
  BindMode = 0
  ClaimChildren = false
  Context = -> Body003 [Import001.]
  FillStyle = 0
  Fuse = false
  MakeFace = false
  PartialLoad = false
  Relative = true
  Support = -> [Body002[Pocket005.Face89]]
  TreeRank = 257
  _Version = 8
FEATURE [PartDesign::SubShapeBinder] Binder007  label="Binder007(Pocket005)"
  BindCopyOnChange = 0
  BindMode = 0
  ClaimChildren = false
  Context = -> Body003 [Binder007.]
  FillStyle = 0
  Fuse = true
  MakeFace = true
  PartialLoad = false
  Refine = true
  Relative = true
  Support = -> [Body002[Pocket005.Face58]]
  TreeRank = 258
  _Version = 8
FEATURE [PartDesign::Pad] Pad005
  AddSubType = 0
  AlongSketchNormal = false
  BaseFeature = -> Pad004
  CheckUpToFaceLimits = true
  ClaimChildren = false
  Direction = (0,0,-1)
  Fit = 0
  FitJoin = 0
  InnerFit = 0
  InnerFitJoin = 0
  InnerTaperAngle = 0
  InnerTaperAngleRev = 0
  Length = 10
  Length2 = 100
  Linearize = true
  NewSolid = false
  Offset = 0.5
  Profile = -> Sketch013
  Refine = true
  Suppress = false
  TreeRank = 259
  Type = 3
  UpToFace = -> Binder007 [Face1]
  _ProfileBasedVersion = 1
FEATURE [Sketcher::SketchObject] Sketch014
  ExternalGeometry = -> [Binder005]
  FullyConstrained = true
  MapMode = 5
  Placement = pos=(0,0,13) rot=(1,0,0;3.14159rad)
  Support = -> [Pad005]
  TreeRank = 260
  sketch-geometry (2):
    g0: Circle CenterX=5.7 CenterY=23.5 CenterZ=0 NormalX=0 NormalY=0 NormalZ=1 AngleXU=0 Radius=2.375
    g1: Circle CenterX=-5.7 CenterY=23.5 CenterZ=0 NormalX=0 NormalY=0 NormalZ=1 AngleXU=0 Radius=2.375
  constraints (4):
    c: Coincident(g0,g-5)
    c: Diameter(g0) = 4.75
    c: Equal(g0,g1) = 4.75
    c: Coincident(g1,g-8)
FEATURE [PartDesign::Pad] Pad006
  AddSubType = 0
  AlongSketchNormal = false
  BaseFeature = -> Pad005
  CheckUpToFaceLimits = true
  ClaimChildren = false
  Direction = (0,0,-1)
  Fit = 0
  FitJoin = 0
  InnerFit = 0
  InnerFitJoin = 0
  InnerTaperAngle = 0
  InnerTaperAngleRev = 0
  Length = 10
  Length2 = 100
  Linearize = true
  NewSolid = false
  Offset = -0.2
  Profile = -> Sketch014
  Refine = true
  Suppress = false
  TreeRank = 261
  Type = 3
  UpToFace = -> Binder006 [Face1]
  _ProfileBasedVersion = 1
FEATURE [Sketcher::SketchObject] Sketch015
  ExternalGeometry = -> [Binder005]
  FullyConstrained = true
  MapMode = 5
  Placement = pos=(0,0,13) rot=(1,0,0;3.14159rad)
  Support = -> [Pad006]
  TreeRank = 262
  sketch-geometry (4):
    g0: Circle CenterX=5.7 CenterY=23.5 CenterZ=0 NormalX=0 NormalY=0 NormalZ=1 AngleXU=0 Radius=1.875
    g1: Circle CenterX=-5.7 CenterY=23.5 CenterZ=0 NormalX=0 NormalY=0 NormalZ=1 AngleXU=0 Radius=1.875
    g2: Circle CenterX=5.7 CenterY=-37.99 CenterZ=0 NormalX=0 NormalY=0 NormalZ=1 AngleXU=0 Radius=1.875
    g3: Circle CenterX=-5.7 CenterY=-37.99 CenterZ=0 NormalX=0 NormalY=0 NormalZ=1 AngleXU=0 Radius=1.875
  constraints (8):
    c: Coincident(g0,g-3)
    c: Diameter(g0) = 3.75
    c: Equal(g0,g1) = 3.75
    c: Coincident(g1,g-4)
    c: Equal(g0,g2) = 3.75
    c: Coincident(g2,g-5)
    c: Equal(g0,g3) = 3.75
    c: Coincident(g3,g-6)
FEATURE [PartDesign::Pocket] Pocket006
  AddSubType = 1
  BaseFeature = -> Pad006
  CheckUpToFaceLimits = true
  ClaimChildren = false
  Fit = 0
  FitJoin = 0
  InnerFit = 0
  InnerFitJoin = 0
  InnerTaperAngle = 0
  InnerTaperAngleRev = 0
  Length = 0
  Length2 = 100
  Linearize = true
  NewSolid = false
  Profile = -> Sketch015
  Refine = true
  Suppress = false
  TreeRank = 263
  Type = 3
  UpToFace = -> Pad006 [Face45]
  _ProfileBasedVersion = 1
  _Version = 1
FEATURE [Sketcher::SketchObject] Sketch016
  ExternalGeometry = -> [Binder005]
  FullyConstrained = true
  MapMode = 5
  Placement = pos=(0,0,15) rot=(0,0,1;0rad)
  Support = -> [Pocket006]
  TreeRank = 264
  sketch-geometry (4):
    g0: Circle CenterX=5.7 CenterY=37.99 CenterZ=0 NormalX=0 NormalY=0 NormalZ=1 AngleXU=0 Radius=1.225
    g1: Circle CenterX=-5.7 CenterY=37.99 CenterZ=0 NormalX=0 NormalY=0 NormalZ=1 AngleXU=0 Radius=1.225
    g2: Circle CenterX=5.7 CenterY=-23.5 CenterZ=0 NormalX=0 NormalY=0 NormalZ=1 AngleXU=0 Radius=1.225
    g3: Circle CenterX=-5.7 CenterY=-23.5 CenterZ=0 NormalX=0 NormalY=0 NormalZ=1 AngleXU=0 Radius=1.225
  constraints (8):
    c: Coincident(g0,g-3)
    c: Diameter(g0) = 2.45
    c: Equal(g0,g1) = 2.4
    c: Coincident(g1,g-4)
    c: Equal(g0,g2) = 2.4
    c: Coincident(g2,g-5)
    c: Equal(g0,g3) = 2.4
    c: Coincident(g3,g-6)
FEATURE [PartDesign::Pocket] Pocket007
  AddSubType = 1
  BaseFeature = -> Pocket006
  CheckUpToFaceLimits = true
  ClaimChildren = false
  Fit = 0
  FitJoin = 0
  InnerFit = 0
  InnerFitJoin = 0
  InnerTaperAngle = 0
  InnerTaperAngleRev = 0
  Length = 0
  Length2 = 100
  Linearize = true
  NewSolid = false
  Profile = -> Sketch016
  Refine = true
  Suppress = false
  TreeRank = 265
  Type = 3
  UpToFace = -> Pocket006 [Face47]
  _ProfileBasedVersion = 1
  _Version = 1
FEATURE [PartDesign::SubShapeBinder] Binder008  label="Binder008(MicroUSB Port, Raspberry Pi Pico-R3)..."
  BindCopyOnChange = 0
  BindMode = 0
  ClaimChildren = false
  Context = -> Body003 [Binder008.]
  FillStyle = 0
  Fuse = false
  MakeFace = true
  PartialLoad = false
  Relative = true
  Support = -> [Part[Raspberry_Pi_Pico_R3.Part__Feature001.Edge368,Raspberry_Pi_Pico_R3.Part__Feature001.Edge436]]
  TreeRank = 266
  _Version = 8
FEATURE [Sketcher::SketchObject] Sketch017
  ExternalGeometry = -> [Binder008,Pocket007]
  FullyConstrained = true
  MapMode = 5
  Placement = pos=(0,0,13) rot=(1,0,0;3.14159rad)
  Support = -> [Pocket007]
  TreeRank = 267
  sketch-geometry (8):
    g0: LineSegment StartX=-4.15 StartY=25.875 StartZ=0 EndX=4.25 EndY=25.875 EndZ=0
    g1: LineSegment StartX=4.25 StartY=25.875 StartZ=0 EndX=4.25 EndY=21.125 EndZ=0
    g2: LineSegment StartX=4.25 StartY=21.125 StartZ=0 EndX=-4.15 EndY=21.125 EndZ=0
    g3: LineSegment StartX=-4.15 StartY=21.125 StartZ=0 EndX=-4.15 EndY=25.875 EndZ=0
    g4: LineSegment [constr] StartX=-5.7 StartY=25.875 StartZ=0 EndX=-4.15 EndY=25.875 EndZ=0
    g5: LineSegment [constr] StartX=4.25 StartY=25.875 StartZ=0 EndX=5.7 EndY=25.875 EndZ=0
    g6: LineSegment [constr] StartX=5.7 StartY=21.125 StartZ=0 EndX=4.25 EndY=21.125 EndZ=0
    g7: LineSegment [constr] StartX=-5.7 StartY=21.125 StartZ=0 EndX=-4.15 EndY=21.125 EndZ=0
  constraints (21):
    c: Coincident(g0,g1)
    c: Coincident(g1,g2)
    c: Coincident(g2,g3)
    c: Coincident(g3,g0)
    c: Horizontal(g0)
    c: Horizontal(g2)
    c: Vertical(g1)
    c: Vertical(g3)
    c: DistanceX(g-3,g0) = 0.5
    c: DistanceX(g0,g-4) = 0.4
    c: Coincident(g4,g0)
    c: Horizontal(g4)
    c: Coincident(g5,g0)
    c: Coincident(g6,g1)
    c: Horizontal(g6)
    c: PointOnObject(g7,g-7)
    c: Coincident(g7,g2)
    c: Horizontal(g7)
    c: Tangent(g4,g-7) = 1.5708
    c: Tangent(g5,g-8) = 1.5708
    c: Tangent(g6,g-8) = 1.5708
FEATURE [PartDesign::Pocket] Pocket008
  AddSubType = 1
  BaseFeature = -> Pocket007
  CheckUpToFaceLimits = true
  ClaimChildren = false
  Fit = 0
  FitJoin = 0
  InnerFit = 0
  InnerFitJoin = 0
  InnerTaperAngle = 0
  InnerTaperAngleRev = 0
  Length = 0
  Length2 = 100
  Linearize = true
  NewSolid = false
  Profile = -> Sketch017
  Refine = true
  Reversed = true
  Suppress = false
  TreeRank = 268
  Type = 3
  UpToFace = -> Pocket007 [Face42]
  _ProfileBasedVersion = 1
  _Version = 1
FEATURE [PartDesign::Body] Body003  label="top_case"
  AutoGroupSolids = false
  BaseFeature = -> BaseFeature001
  ExportMode = 0
  Group = -> [BaseFeature001,Chamfer003,Sketch006,Pocket001,Sketch007,Pocket002,Binder005,Sketch012,Binder006,Pad004,Sketch013,Import001,Binder007,Pad005,Sketch014,Pad006,Sketch015,Pocket006,Sketch016,Pocket007,Binder008,Sketch017,Pocket008]
  Origin = -> Origin005
  Tip = -> Pocket008
  TreeRank = 228
  _ExportChildren = -> [BaseFeature001,Chamfer003,Pocket001,Pocket002,Binder005,Binder006,Pad004,Import001,Binder007,Pad005,Pad006,Pocket006,Pocket007,Binder008,Pocket008]
  _GroupVersion = 1
FEATURE [Mesh::Feature] Mesh  label="bottom_case (Meshed)"
  TreeRank = 269
FEATURE [Mesh::Feature] Mesh001  label="top_case (Meshed)"
  TreeRank = 270
FEATURE [App::Part] Part  label="Pi_case"
  ExportMode = 1
  Group = -> [Raspberry_Pi_Pico_R3,Body]
  Origin = -> Origin001
  TreeRank = 143
  _ExportChildren = -> [Raspberry_Pi_Pico_R3,Body]
  _GroupVersion = 1
FEATURE [PartDesign::Body] Body
  AutoGroupSolids = false
  ExportMode = 0
  Group = -> [Binder,Sketch,Pad,Thickness,Binder001,Pad001,Binder002,Sketch001,Pocket,Binder003,Pad002,Fillet,Fillet001,Chamfer,Chamfer001,Split,Import,Split_i0,Split_i1]
  Origin = -> Origin002
  Tip = -> Split
  TreeRank = 155
  _ExportChildren = -> [Binder,Pad,Thickness,Pad001,Binder002,Pocket,Pad002,Fillet,Fillet001,Chamfer,Chamfer001,Split]
  _GroupVersion = 1
FEATURE [PartDesign::Split] Split
  BaseFeature = -> Chamfer001
  Fragment = false
  Mode = 0
  NewSolid = false
  Solids = -> [Split_i0,Split_i1]
  Suppress = false
  Tolerance = 0
  Tools = -> [Import]
  TreeRank = 203
  _Version = 1
FEATURE [PartDesign::Solid] Split_i0
  Active = true
  Parent = -> Split
  TreeRank = 201
FEATURE [PartDesign::Solid] Split_i1
  Active = true
  Parent = -> Split
  TreeRank = 202
